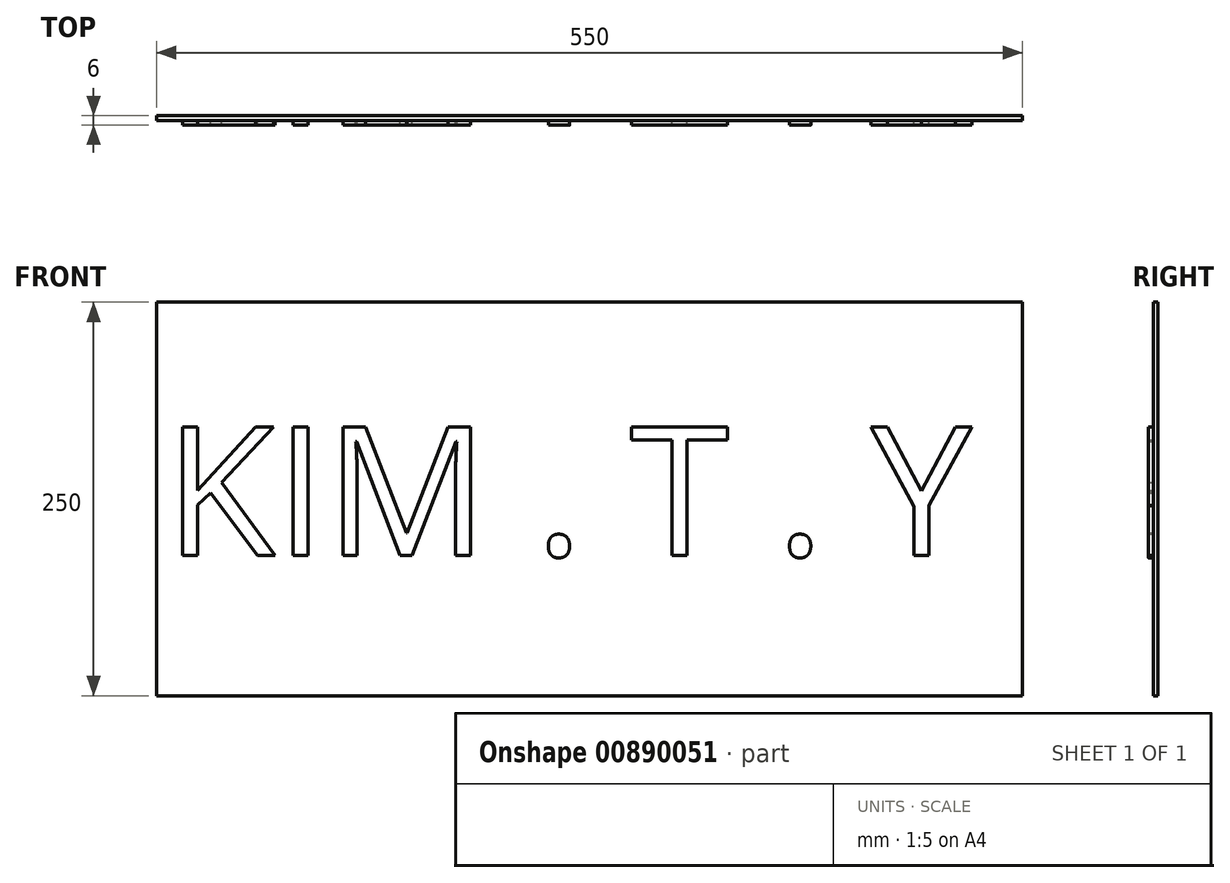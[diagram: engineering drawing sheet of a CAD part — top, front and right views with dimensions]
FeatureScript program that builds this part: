
annotation { "Feature Type Name" : "Feature", "Feature Type Description" : "" }
export const myFeature = defineFeature(function(context is Context, id is Id, definition is map)
    precondition{}
    {
        {
            var Q0;
            Q0=qCreatedBy(makeId("Front.planeOp"),FACE);
            var sketch = newSketch(context, id + "F0", { "sketchPlane" : qUnion([Q0])});
            skLineSegment(sketch, "E0.bottom", {"start": v(0, 0) * mm, "end": v(550, 0) * mm});
            skLineSegment(sketch, "E0.top", {"start": v(0, 250) * mm, "end": v(550, 250) * mm});
            skLineSegment(sketch, "E0.left", {"start": v(0, 0) * mm, "end": v(0, 250) * mm});
            skLineSegment(sketch, "E0.right", {"start": v(550, 0) * mm, "end": v(550, 250) * mm});
            skSolve(sketch);
        }
        {
            var Q0;
            Q0=makeQuery(id+"F0.imprint","IMPRINT",FACE,{"disambiguationData":[TD([[makeQuery(id+"F0.imprint","IMPRINT",EDGE,{"derivedFrom":sQuery(id+"F0.wireOp",EDGE,"E0.bottom")}),1.0]])]});
            extrude(context, id + "F1", {"entities" : qUnion([Q0]), "depth" : 3 * mm, "offsetDistance" : 25 * mm});
        }
        {
            var Q0;
            Q0=makeQuery(id+"F1.opExtrude","CAP_FACE",FACE,{"disambiguationData":[OSD([sQuery(id+"F0.wireOp",EDGE,"E0.bottom"),sQuery(id+"F0.wireOp",EDGE,"E0.top"),sQuery(id+"F0.wireOp",EDGE,"E0.left"),sQuery(id+"F0.wireOp",EDGE,"E0.right")])],"isStart":false});
            var sketch = newSketch(context, id + "F2", { "sketchPlane" : qUnion([Q0])});
            skText(sketch, "E1", { "text": "KIM . T . Y", "fontName": "OpenSans-Regular.ttf"});
            const initialGuessF2  = {"E1": [0.00523, 0.0892, 1, 0, 0.08238]};
            skSetInitialGuess(sketch, initialGuessF2);
            skSolve(sketch);
        }
        {
            var Q0;
            Q0 = qSketchRegion(id + "F2", true);
            extrude(context, id + "F3", {"entities" : qUnion([Q0]), "operationType" : NewBodyOperationType.ADD, "depth" : 3 * mm, "offsetDistance" : 25 * mm});
        }
    });
